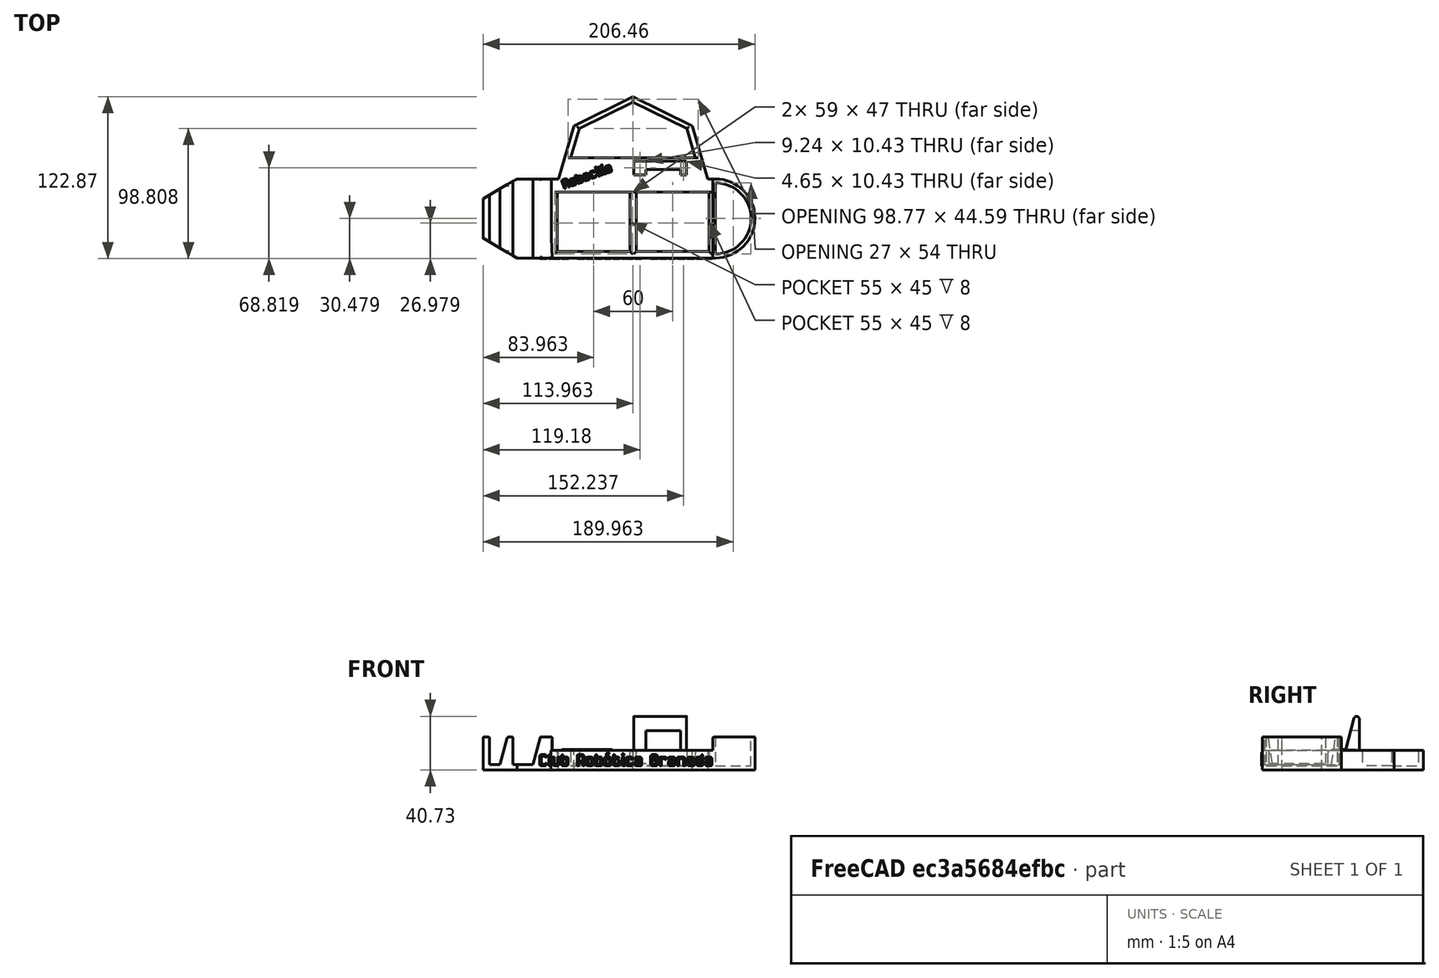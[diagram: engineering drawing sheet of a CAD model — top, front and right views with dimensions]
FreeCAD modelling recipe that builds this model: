
FCSTD DOCUMENT  (FreeCAD 0.19R24276 (Git))
Label: tarjetero
License: All rights reserved
LicenseURL: http://en.wikipedia.org/wiki/All_rights_reserved
objects: Sketcher::SketchObject×12, PartDesign::Fillet×7, PartDesign::Pad×6, PartDesign::Pocket×6, Part::Part2DObjectPython×2, Part::Extrusion×2, Part::MultiFuse×2, App::DocumentObjectGroup×2, PartDesign::Plane×1, PartDesign::Body×1, Mesh::Feature×1, Part::Feature×1
note: 59 computed .brp shape members not serialized (recipe doc carries the construction recipe); baked Part::Feature solids carry a one-line shape summary decoded from their .brp

FEATURE [Sketcher::SketchObject] Sketch008
  FullyConstrained = false
  MapMode = 5
  Support = -> [XY_Plane006]
  sketch-geometry (4):
    g0: LineSegment StartX=35.2534 StartY=106.479 StartZ=0 EndX=160.253 EndY=106.479 EndZ=0
    g1: LineSegment StartX=160.253 StartY=106.479 StartZ=0 EndX=160.253 EndY=46.4789 EndZ=0
    g2: LineSegment StartX=160.253 StartY=46.4789 StartZ=0 EndX=35.2534 EndY=46.4789 EndZ=0
    g3: LineSegment StartX=35.2534 StartY=46.4789 StartZ=0 EndX=35.2534 EndY=106.479 EndZ=0
  constraints (10):
    c: Coincident(g0,g1)
    c: Coincident(g1,g2)
    c: Coincident(g2,g3)
    c: Coincident(g3,g0)
    c: Horizontal(g0)
    c: Horizontal(g2)
    c: Vertical(g1)
    c: Vertical(g3)
    c: DistanceX(g2,g2) = 125
    c: DistanceY(g1,g1) = 60
FEATURE [PartDesign::Pad] Pad007
  Direction = (1,1,1)
  Length = 15
  Length2 = 100
  Profile = -> Sketch008
  Refine = true
  Type = 0
FEATURE [Sketcher::SketchObject] Sketch009
  ExternalGeometry = -> [Pad007]
  FullyConstrained = true
  MapMode = 5
  Placement = pos=(0,0,15) rot=(0,0,1;0rad)
  Support = -> [Pad007]
  sketch-geometry (4):
    g0: LineSegment StartX=40.2534 StartY=96.4789 StartZ=0 EndX=155.253 EndY=96.4789 EndZ=0
    g1: LineSegment StartX=155.253 StartY=96.4789 StartZ=0 EndX=155.253 EndY=51.4789 EndZ=0
    g2: LineSegment StartX=155.253 StartY=51.4789 StartZ=0 EndX=40.2534 EndY=51.4789 EndZ=0
    g3: LineSegment StartX=40.2534 StartY=51.4789 StartZ=0 EndX=40.2534 EndY=96.4789 EndZ=0
  constraints (12):
    c: Coincident(g0,g1)
    c: Coincident(g1,g2)
    c: Coincident(g2,g3)
    c: Coincident(g3,g0)
    c: Horizontal(g0)
    c: Horizontal(g2)
    c: Vertical(g1)
    c: Vertical(g3)
    c: DistanceY(g-3,g2) = 5
    c: DistanceX(g-3,g2) = 5
    c: DistanceX(g1,g-4) = 5
    c: DistanceY(g0,g-4) = 10
FEATURE [PartDesign::Pocket] Pocket001
  BaseFeature = -> Pad007
  Length = 10
  Length2 = 100
  Profile = -> Sketch009
  Refine = true
  Type = 0
FEATURE [Sketcher::SketchObject] Sketch010
  ExternalGeometry = -> [Pocket001]
  FullyConstrained = true
  MapMode = 5
  Placement = pos=(0,0,5) rot=(0,0,1;0rad)
  Support = -> [Pocket001]
  sketch-geometry (5):
    g0: LineSegment StartX=97.7534 StartY=96.4789 StartZ=0 EndX=97.7534 EndY=51.4789 EndZ=0
    g1: LineSegment StartX=95.2534 StartY=96.4789 StartZ=0 EndX=100.253 EndY=96.4789 EndZ=0
    g2: LineSegment StartX=100.253 StartY=96.4789 StartZ=0 EndX=100.253 EndY=51.4789 EndZ=0
    g3: LineSegment StartX=100.253 StartY=51.4789 StartZ=0 EndX=95.2534 EndY=51.4789 EndZ=0
    g4: LineSegment StartX=95.2534 StartY=51.4789 StartZ=0 EndX=95.2534 EndY=96.4789 EndZ=0
  constraints (14):
    c: Vertical(g0)
    c: PointOnObject(g0,g-4)
    c: Symmetric(g-3,g-3,g0)
    c: Coincident(g1,g2)
    c: Coincident(g2,g3)
    c: Coincident(g3,g4)
    c: Coincident(g4,g1)
    c: Horizontal(g1)
    c: Vertical(g2)
    c: Vertical(g4)
    c: PointOnObject(g1,g-3)
    c: PointOnObject(g2,g-4)
    c: Symmetric(g3,g2,g0)
    c: DistanceX(g1,g1) = 5
FEATURE [PartDesign::Pad] Pad008  label="centro"
  BaseFeature = -> Pocket001
  Direction = (1,1,1)
  Length = 10
  Length2 = 100
  Profile = -> Sketch010
  Refine = true
  Type = 0
FEATURE [Sketcher::SketchObject] Sketch011
  ExternalGeometry = -> [Pad008]
  FullyConstrained = false
  MapMode = 5
  Placement = pos=(0,0,0) rot=(1,0,0;3.14159rad)
  Support = -> [Pad008]
  sketch-geometry (6):
    g0: LineSegment StartX=40.2534 StartY=-103.479 StartZ=0 EndX=155.253 EndY=-103.479 EndZ=0
    g1: LineSegment StartX=40.2534 StartY=-103.479 StartZ=0 EndX=52.9636 EndY=-146.647 EndZ=0
    g2: LineSegment StartX=52.9636 StartY=-146.647 StartZ=0 EndX=97.7534 EndY=-168.87 EndZ=0
    g3: LineSegment StartX=97.7534 StartY=-168.87 StartZ=0 EndX=142.543 EndY=-146.647 EndZ=0
    g4: LineSegment StartX=142.543 StartY=-146.647 StartZ=0 EndX=155.253 EndY=-103.479 EndZ=0
    g5: LineSegment StartX=97.7534 StartY=-168.87 StartZ=0 EndX=97.7534 EndY=-103.479 EndZ=0
  constraints (15):
    c: Horizontal(g0)
    c: Coincident(g0,g1)
    c: Coincident(g1,g2)
    c: Coincident(g2,g3)
    c: Coincident(g3,g4)
    c: Coincident(g4,g0)
    c: Coincident(g5,g2)
    c: PointOnObject(g5,g0)
    c: Symmetric(g0,g0,g5)
    c: Symmetric(g1,g3,g5)
    c: DistanceX(g-3,g0) = 5
    c: DistanceX(g0,g-3) = 5
    c: DistanceY(g-3,g0) = 3
    c: Distance(g1) = 45
    c: Distance(g3) = 50
FEATURE [PartDesign::Pad] Pad009
  BaseFeature = -> Pad008
  Direction = (1,1,1)
  Length = 15
  Length2 = 100
  Profile = -> Sketch011
  Refine = true
  Reversed = true
  Type = 0
FEATURE [Sketcher::SketchObject] Sketch012
  ExternalGeometry = -> [Pad009]
  FullyConstrained = false
  MapMode = 5
  Placement = pos=(0,0,0) rot=(1,0,0;3.14159rad)
  Support = -> [Pad009]
  sketch-geometry (11):
    g0: LineSegment StartX=35.7534 StartY=-91.4789 StartZ=0 EndX=35.7534 EndY=-61.4789 EndZ=0
    g1: LineSegment StartX=9.76466 StartY=-46.4789 StartZ=0 EndX=-16.2081 EndY=-61.4789 EndZ=0
    g2: LineSegment StartX=-16.2081 StartY=-61.4789 StartZ=0 EndX=-16.2081 EndY=-91.4789 EndZ=0
    g3: LineSegment StartX=-16.2081 StartY=-91.4789 StartZ=0 EndX=9.76467 EndY=-106.479 EndZ=0
    g4: Circle CenterX=9.77262 CenterY=-76.4789 CenterZ=0 NormalX=0 NormalY=0 NormalZ=1 AngleXU=0 Radius=30
    g5: LineSegment StartX=35.2534 StartY=-76.4789 StartZ=0 EndX=160.253 EndY=-76.4789 EndZ=0
    g6: LineSegment StartX=97.7534 StartY=-63.6246 StartZ=0 EndX=97.7534 EndY=-87.2392 EndZ=0
    g7: LineSegment StartX=35.7534 StartY=-61.4789 StartZ=0 EndX=36.3881 EndY=-46.4789 EndZ=0
    g8: LineSegment StartX=36.3881 StartY=-46.4789 StartZ=0 EndX=9.76466 EndY=-46.4789 EndZ=0
    g9: LineSegment StartX=35.7534 StartY=-91.4789 StartZ=0 EndX=35.7534 EndY=-106.479 EndZ=0
    g10: LineSegment StartX=35.7534 StartY=-106.479 StartZ=0 EndX=9.76467 EndY=-106.479 EndZ=0
  constraints (26):
    c: Coincident(g1,g2)
    c: Coincident(g2,g3)
    c: PointOnObject(g0,g4)
    c: PointOnObject(g0,g4)
    c: PointOnObject(g1,g4)
    c: PointOnObject(g1,g4)
    c: PointOnObject(g2,g4)
    c: PointOnObject(g3,g4)
    c: Vertical(g2)
    c: PointOnObject(g5,g-3)
    c: PointOnObject(g5,g-4)
    c: Symmetric(g-3,g-3,g5)
    c: DistanceY(g-3,g-3) = 60
    c: Radius(g4) = 30
    c: Symmetric(g5,g5,g6)
    c: DistanceX(g-3,g0) = 0.5
    c: Symmetric(g0,g0,g5)
    c: Coincident(g0,g7)
    c: Coincident(g7,g8)
    c: Coincident(g8,g1)
    c: Horizontal(g8)
    c: Coincident(g0,g9)
    c: Vertical(g9)
    c: Coincident(g9,g10)
    c: Coincident(g10,g3)
    c: Horizontal(g10)
FEATURE [PartDesign::Pad] Pad010
  BaseFeature = -> Pad009
  Direction = (1,1,1)
  Length = 25
  Length2 = 100
  Profile = -> Sketch012
  Refine = true
  Reversed = true
  Type = 0
FEATURE [Sketcher::SketchObject] Sketch014
  ExternalGeometry = -> [Pad010]
  FullyConstrained = false
  MapMode = 5
  Placement = pos=(0,46.4789,0) rot=(1,0,0;1.5708rad)
  Support = -> [Pad010]
  sketch-geometry (5):
    g0: LineSegment StartX=21.6256 StartY=4 StartZ=0 EndX=31.0147 EndY=39.0405 EndZ=0
    g1: LineSegment StartX=31.0147 StartY=39.0405 StartZ=0 EndX=16.0147 EndY=39.0405 EndZ=0
    g2: LineSegment StartX=6.62563 StartY=4 StartZ=0 EndX=21.6256 EndY=4 EndZ=0
    g3: LineSegment StartX=6.62563 StartY=4 StartZ=0 EndX=6.62563 EndY=34.4782 EndZ=0
    g4: LineSegment StartX=6.62563 StartY=34.4782 StartZ=0 EndX=16.0147 EndY=39.0405 EndZ=0
  constraints (10):
    c: Coincident(g0,g1)
    c: Horizontal(g1)
    c: Coincident(g2,g0)
    c: Horizontal(g2)
    c: DistanceY(g-3,g0) = 4
    c: DistanceX(g2,g2) = 15
    c: Coincident(g3,g2)
    c: Vertical(g3)
    c: Coincident(g4,g3)
    c: Coincident(g4,g1)
FEATURE [PartDesign::Pocket] Pocket002
  BaseFeature = -> Pad010
  Length = 5
  Length2 = 100
  Profile = -> Sketch014
  Refine = true
  Type = 1
FEATURE [Sketcher::SketchObject] Sketch015
  FullyConstrained = false
  MapMode = 5
  Placement = pos=(0,46.4789,0) rot=(1,0,0;1.5708rad)
  Support = -> [Pocket002]
  sketch-geometry (4):
    g0: LineSegment StartX=2.97068 StartY=27.1215 StartZ=0 EndX=-3.22471 EndY=4 EndZ=0
    g1: LineSegment StartX=-3.22471 StartY=4 StartZ=0 EndX=-11.2247 EndY=4 EndZ=0
    g2: LineSegment StartX=-11.2247 StartY=4 StartZ=0 EndX=-11.2247 EndY=27.1215 EndZ=0
    g3: LineSegment StartX=-11.2247 StartY=27.1215 StartZ=0 EndX=2.97068 EndY=27.1215 EndZ=0
  constraints (10):
    c: Coincident(g0,g1)
    c: Horizontal(g1)
    c: Coincident(g1,g2)
    c: Vertical(g2)
    c: Coincident(g2,g3)
    c: Coincident(g3,g0)
    c: Horizontal(g3)
    c: Angle(g0,g-2) = 0.261799
    c: DistanceY(g-1,g0) = 4
    c: DistanceX(g1,g1) = 8
FEATURE [PartDesign::Pocket] Pocket003  label="tarjetero-base-posterior"
  BaseFeature = -> Pocket002
  Length = 62
  Length2 = 100
  Profile = -> Sketch015
  Refine = true
  Type = 0
FEATURE [Sketcher::SketchObject] Sketch016
  ExternalGeometry = -> [Pocket003]
  FullyConstrained = true
  MapMode = 5
  Placement = pos=(0,0,0) rot=(1,0,0;3.14159rad)
  Support = -> [Pocket003]
  sketch-geometry (4):
    g0: ArcOfCircle CenterX=160.253 CenterY=-76.4789 CenterZ=0 NormalX=0 NormalY=0 NormalZ=1 AngleXU=0 Radius=30 StartAngle=4.71239 EndAngle=7.85398
    g1: LineSegment StartX=160.253 StartY=-46.4789 StartZ=0 EndX=158.253 EndY=-46.4789 EndZ=0
    g2: LineSegment StartX=158.253 StartY=-46.4789 StartZ=0 EndX=158.253 EndY=-106.479 EndZ=0
    g3: LineSegment StartX=158.253 StartY=-106.479 StartZ=0 EndX=160.253 EndY=-106.479 EndZ=0
  constraints (11):
    c: PointOnObject(g0,g-3)
    c: Coincident(g0,g-3)
    c: Coincident(g0,g-3)
    c: Coincident(g1,g2)
    c: Coincident(g2,g3)
    c: Horizontal(g1)
    c: Horizontal(g3)
    c: Vertical(g2)
    c: Coincident(g1,g0)
    c: Coincident(g3,g0)
    c: DistanceX(g1,g0) = 2
FEATURE [PartDesign::Pad] Pad011
  BaseFeature = -> Pocket003
  Direction = (1,1,1)
  Length = 25
  Length2 = 100
  Profile = -> Sketch016
  Refine = true
  Reversed = true
  Type = 0
FEATURE [Sketcher::SketchObject] Sketch017
  ExternalGeometry = -> [Pad011]
  FullyConstrained = false
  MapMode = 5
  Placement = pos=(0,0,25) rot=(0,0,1;0rad)
  Support = -> [Pad011]
  sketch-geometry (2):
    g0: ArcOfCircle CenterX=160.253 CenterY=76.4789 CenterZ=0 NormalX=0 NormalY=0 NormalZ=1 AngleXU=0 Radius=27 StartAngle=4.71239 EndAngle=7.85398
    g1: LineSegment StartX=160.253 StartY=103.479 StartZ=0 EndX=160.253 EndY=49.4789 EndZ=0
  constraints (4):
    c: Coincident(g0,g-3)
    c: Coincident(g1,g0)
    c: Coincident(g1,g0)
    c: DistanceY(g0,g-3) = 3
FEATURE [PartDesign::Pocket] Pocket004
  BaseFeature = -> Pad011
  Length = 22
  Length2 = 100
  Profile = -> Sketch017
  Refine = true
  Type = 0
FEATURE [PartDesign::Fillet] Fillet006  label="Fillet009"
  Base = -> Pocket004 [Edge84]
  BaseFeature = -> Pocket004
  Radius = 1
  Refine = true
  SupportTransform = false
FEATURE [PartDesign::Fillet] Fillet007  label="Fillet010"
  Base = -> Fillet006 [Face35]
  BaseFeature = -> Fillet006
  Radius = 1
  Refine = true
  SupportTransform = false
FEATURE [PartDesign::Fillet] Fillet008  label="Fillet011"
  Base = -> Fillet007 [Face23]
  BaseFeature = -> Fillet007
  Radius = 1
  Refine = true
  SupportTransform = false
FEATURE [PartDesign::Fillet] Fillet009  label="Fillet012"
  Base = -> Fillet008 [Face8]
  BaseFeature = -> Fillet008
  Radius = 1
  Refine = true
  SupportTransform = false
FEATURE [PartDesign::Fillet] Fillet010  label="frontal-completa"
  Base = -> Fillet009 [Edge114,Edge115,Edge112,Edge111,Edge109,Edge108]
  BaseFeature = -> Fillet009
  Radius = 2
  Refine = true
  SupportTransform = false
FEATURE [PartDesign::Plane] DatumPlane
  AttachmentOffset = pos=(-41,0,0) rot=(0,1,0;1.5708rad)
  Length = 64.2463
  MapMode = 45
  Placement = pos=(138.352,76.4789,12.5) rot=(0,1,0;1.5708rad)
  ResizeMode = 0
  Support = -> [Pad011]
  Width = 115.725
FEATURE [Sketcher::SketchObject] Sketch018
  FullyConstrained = false
  MapMode = 5
  Placement = pos=(138.352,76.4789,12.5) rot=(0,1,0;1.5708rad)
  Support = -> [DatumPlane]
  sketch-geometry (3):
    g0: LineSegment StartX=0 StartY=32.4552 StartZ=0 EndX=-41.4237 EndY=43.5546 EndZ=0
    g1: LineSegment StartX=-41.4237 StartY=43.5546 StartZ=0 EndX=0 EndY=43.5546 EndZ=0
    g2: LineSegment StartX=0 StartY=43.5546 StartZ=0 EndX=0 EndY=32.4552 EndZ=0
  constraints (7):
    c: PointOnObject(g0,g-2)
    c: Coincident(g0,g1)
    c: Horizontal(g1)
    c: Coincident(g1,g2)
    c: Coincident(g2,g0)
    c: Vertical(g2)
    c: Angle(g0,g1) = 0.261799
FEATURE [PartDesign::Pad] Pad012
  BaseFeature = -> Fillet010
  Direction = (1,1,1)
  Length = 40
  Length2 = 100
  Profile = -> Sketch018
  Refine = true
  Reversed = true
  Type = 0
FEATURE [Sketcher::SketchObject] Sketch019
  ExternalGeometry = -> [Pad012]
  FullyConstrained = false
  MapMode = 5
  Placement = pos=(0,120.034,0) rot=(0,0.707107,0.707107;3.14159rad)
  Support = -> [Pad012]
  sketch-geometry (4):
    g0: LineSegment StartX=-133.702 StartY=15 StartZ=0 EndX=-107.589 EndY=15 EndZ=0
    g1: LineSegment StartX=-107.589 StartY=15 StartZ=0 EndX=-107.589 EndY=29.6378 EndZ=0
    g2: LineSegment StartX=-107.589 StartY=29.6378 StartZ=0 EndX=-133.702 EndY=29.6378 EndZ=0
    g3: LineSegment StartX=-133.702 StartY=29.6378 StartZ=0 EndX=-133.702 EndY=15 EndZ=0
  constraints (9):
    c: Horizontal(g0)
    c: Coincident(g0,g1)
    c: Vertical(g1)
    c: Coincident(g1,g2)
    c: Horizontal(g2)
    c: Coincident(g2,g3)
    c: Coincident(g3,g0)
    c: Vertical(g3)
    c: DistanceY(g0,g-3) = 0
FEATURE [PartDesign::Pocket] Pocket005  label="soporte-adherir"
  BaseFeature = -> Pad012
  Length = 11
  Length2 = 100
  Profile = -> Sketch019
  Refine = true
  Type = 0
FEATURE [Sketcher::SketchObject] Sketch020
  ExternalGeometry = -> [Pocket005]
  FullyConstrained = false
  MapMode = 5
  Placement = pos=(0,0,15) rot=(0,0,1;0rad)
  Support = -> [Pocket005]
  sketch-geometry (5):
    g0: LineSegment StartX=50.451 StartY=122.513 StartZ=0 EndX=145.056 EndY=122.513 EndZ=0
    g1: LineSegment StartX=145.056 StartY=122.513 StartZ=0 EndX=138.543 EndY=144.631 EndZ=0
    g2: LineSegment StartX=138.543 StartY=144.631 StartZ=0 EndX=97.7534 EndY=164.87 EndZ=0
    g3: LineSegment StartX=97.7534 StartY=164.87 StartZ=0 EndX=56.9636 EndY=144.631 EndZ=0
    g4: LineSegment StartX=56.9636 StartY=144.631 StartZ=0 EndX=50.451 EndY=122.513 EndZ=0
  constraints (14):
    c: Horizontal(g0)
    c: Coincident(g0,g1)
    c: Coincident(g1,g2)
    c: Coincident(g2,g3)
    c: Coincident(g3,g4)
    c: Coincident(g4,g0)
    c: Parallel(g-3,g4)
    c: Parallel(g-4,g3)
    c: Parallel(g2,g-5)
    c: Parallel(g1,g-6)
    c: DistanceX(g-5,g2) = 0
    c: Equal(g3,g2)
    c: DistanceX(g-4,g3) = 4
    c: DistanceY(g2,g-5) = 4
FEATURE [PartDesign::Pocket] Pocket006  label="vaciado-posterior"
  BaseFeature = -> Pocket005
  Length = 12
  Length2 = 100
  Profile = -> Sketch020
  Refine = true
  Type = 0
FEATURE [PartDesign::Fillet] Fillet011  label="Fillet014"
  Base = -> Pocket006 [Edge57,Edge56,Edge55,Edge54]
  BaseFeature = -> Pocket006
  Radius = 2
  Refine = true
  SupportTransform = false
FEATURE [PartDesign::Fillet] Fillet012  label="final-sin-letras"
  Base = -> Fillet011 [Edge117]
  BaseFeature = -> Fillet011
  Radius = 2
  Refine = true
  SupportTransform = false
FEATURE [PartDesign::Body] Body006  label="diseño-base-sin-letras"
  Group = -> [Sketch008,Pad007,Sketch009,Pocket001,Sketch010,Pad008,Sketch011,Pad009,Sketch012,Pad010,Sketch014,Pocket002,Sketch015,Pocket003,Sketch016,Pad011,Sketch017,Pocket004,Fillet006,Fillet007,Fillet008,Fillet009,Fillet010,DatumPlane,Sketch018,Pad012,Sketch019,Pocket005,Sketch020,Pocket006,Fillet011,Fillet012]
  Origin = -> Origin006
  Tip = -> Fillet012
FEATURE [Part::Part2DObjectPython] ShapeString001  # Draft 2D object (typed FeaturePython)
  FontFile = <userpath>/3D/tabla-periodica/3D/src/Sircuito-Regular-Bold.ttf
  Placement = pos=(26.67,48,3.1) rot=(1,0,0;1.5708rad)
  Size = 5
  String = Club Robótica Granada
  Tracking = 0
FEATURE [Part::Extrusion] Extrude001
  Base = -> ShapeString001
  Dir = (0,-1,2e-16)
  DirMode = 2
  FaceMakerClass = Part::FaceMakerBullseye
  LengthFwd = 2
  LengthRev = 0
  Solid = true
  Symmetric = false
FEATURE [Part::MultiFuse] Fusion003  label="CRG"
  Refine = true
  Shapes = -> [Extrude001,Fillet012]
FEATURE [Part::Part2DObjectPython] ShapeString002  # Draft 2D object (typed FeaturePython)
  FontFile = <userpath>/3D/tabla-periodica/3D/src/Sircuito-Regular-Bold.ttf
  Placement = pos=(45.67,99,14.1) rot=(0,0,1;0.349066rad)
  Size = 4
  String = Robocilio
  Tracking = 0
FEATURE [Part::Extrusion] Extrude002
  Base = -> ShapeString002
  Dir = (0,0,1)
  DirMode = 2
  FaceMakerClass = Part::FaceMakerBullseye
  LengthFwd = 1.5
  LengthRev = 0
  Solid = true
  Symmetric = false
FEATURE [Part::MultiFuse] Fusion004  label="tarjetero"
  Refine = true
  Shapes = -> [Extrude002,Fusion003]
FEATURE [Mesh::Feature] Robocilio_170  label="Robocilio-170"
  Placement = pos=(-19,104.25,-5) rot=(1,0,0;1.309rad)
FEATURE [App::DocumentObjectGroup] Grupo  label="src"
  Group = -> [Fusion004,Body006]
FEATURE [Part::Feature] Fusion004001  label="tarjetero-c"
  shape: bbox 206.5 x 122.9 x 40.73 mm, 861 faces (baked)
FEATURE [App::DocumentObjectGroup] Grupo001  label="montaje"
  Group = -> [Fusion004001,Robocilio_170]
